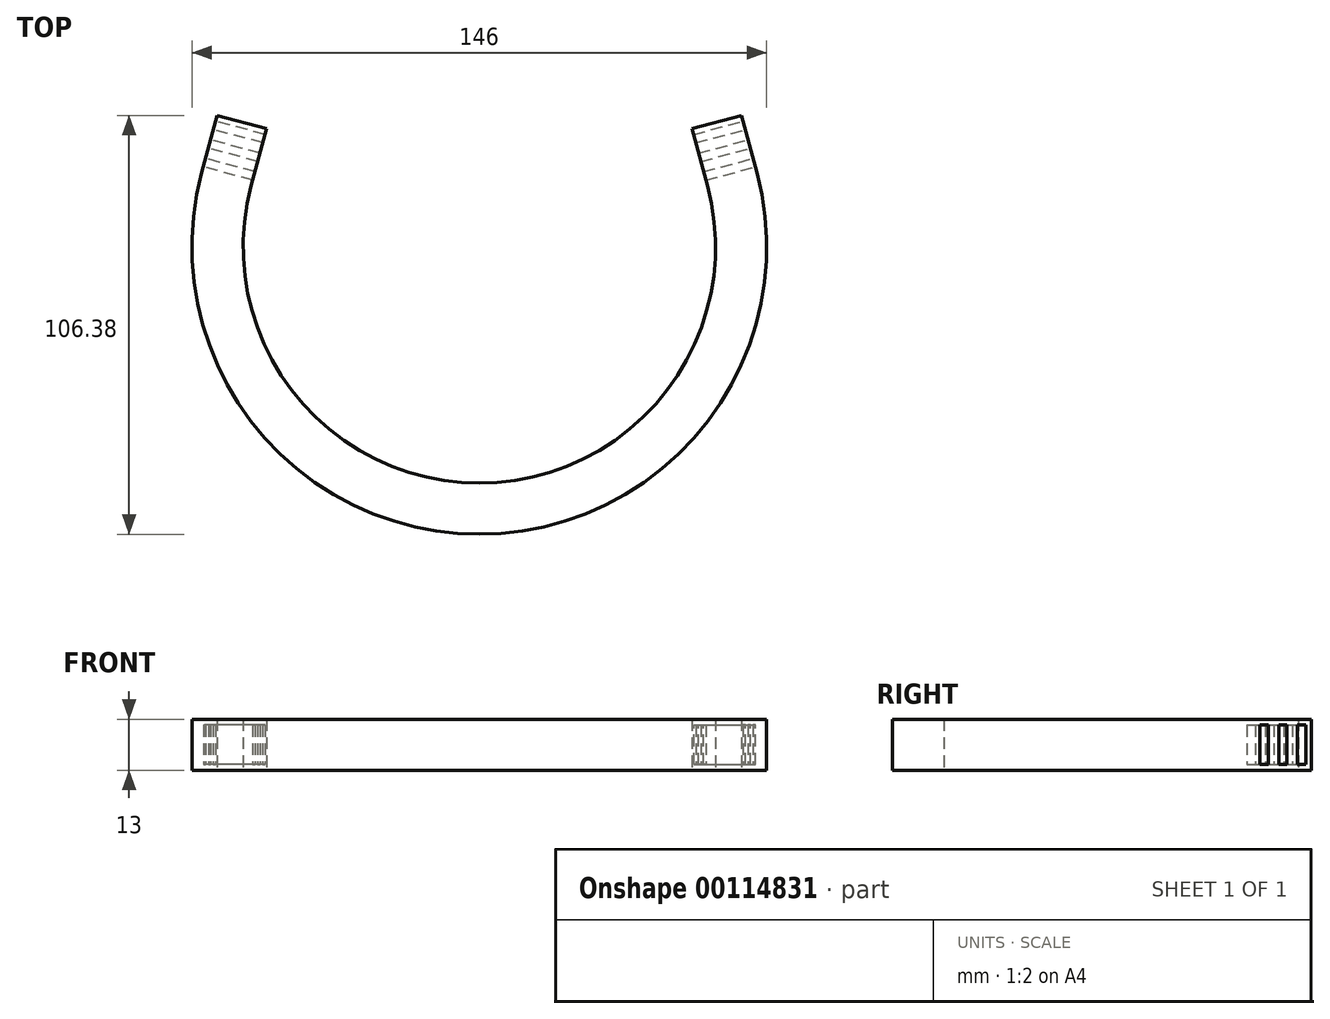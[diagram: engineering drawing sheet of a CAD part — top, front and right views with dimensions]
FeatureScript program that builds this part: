
annotation { "Feature Type Name" : "Feature", "Feature Type Description" : "" }
export const myFeature = defineFeature(function(context is Context, id is Id, definition is map)
    precondition{}
    {
        {
            var Q0;
            Q0=qCreatedBy(makeId("Top.planeOp"),FACE);
            var sketch = newSketch(context, id + "F0", { "sketchPlane" : qUnion([Q0])});
            skArc(sketch, "E0", {"start": v(-57.96, 15.53) * mm, "mid": v(0, -60) * mm, "end": v(57.96, 15.53) * mm});
            skArc(sketch, "E1.0", {"start": v(-70.51, 18.9) * mm, "mid": v(0, -73) * mm, "end": v(70.51, 18.9) * mm});
            skLineSegment(sketch, "E2", {"start": v(0, 0) * mm, "end": v(57.96, 15.53) * mm, "construction": true});
            skLineSegment(sketch, "E3.MirrorCS", {"start": v(0, 0) * mm, "end": v(-57.96, 15.53) * mm, "construction": true});
            skLineSegment(sketch, "E4", {"start": v(-70.51, 18.9) * mm, "end": v(-66.63, 33.38) * mm});
            skLineSegment(sketch, "E5", {"start": v(-57.96, 15.53) * mm, "end": v(-54.07, 30.02) * mm});
            skLineSegment(sketch, "E6", {"start": v(-54.07, 30.02) * mm, "end": v(-66.63, 33.38) * mm});
            skLineSegment(sketch, "E7.MirrorCS", {"start": v(54.07, 30.02) * mm, "end": v(66.63, 33.38) * mm});
            skLineSegment(sketch, "E8.MirrorCS", {"start": v(57.96, 15.53) * mm, "end": v(54.07, 30.02) * mm});
            skLineSegment(sketch, "E9.MirrorCS", {"start": v(70.51, 18.9) * mm, "end": v(66.63, 33.38) * mm});
            skLineSegment(sketch, "E10.trimOffspring", {"start": v(70.51, 18.9) * mm, "end": v(130.04, 34.84) * mm, "construction": true});
            skLineSegment(sketch, "E11.trimOffspring", {"start": v(-70.51, 18.9) * mm, "end": v(-130.04, 34.84) * mm, "construction": true});
            skSolve(sketch);
        }
        {
            var Q0;
            Q0=makeQuery(id+"F0.imprint","IMPRINT",FACE,{"disambiguationData":[TD([[makeQuery(id+"F0.imprint","IMPRINT",EDGE,{"derivedFrom":sQuery(id+"F0.wireOp",EDGE,"E1.0")}),1.0]])]});
            extrude(context, id + "F1", {"entities" : qUnion([Q0]), "depth" : 13 * mm});
        }
        {
            var Q0;
            Q0=makeQuery(id+"F1.opExtrude","SWEPT_FACE",FACE,{"disambiguationData":[OSD([sQuery(id+"F0.wireOp",EDGE,"E9.MirrorCS")])]});
            var sketch = newSketch(context, id + "F2", { "sketchPlane" : qUnion([Q0])});
            skLineSegment(sketch, "E12", {"start": v(12.98, 7.6) * mm, "end": v(12.98, 5.4) * mm});
            skLineSegment(sketch, "E13", {"start": v(0, 5.4) * mm, "end": v(0, 7.6) * mm});
            skLineSegment(sketch, "E14", {"start": v(1.5, 7.6) * mm, "end": v(1.5, 11.5) * mm});
            skLineSegment(sketch, "E15", {"start": v(1.5, 11.5) * mm, "end": v(3.7, 11.5) * mm});
            skLineSegment(sketch, "E16", {"start": v(3.7, 11.5) * mm, "end": v(3.7, 7.6) * mm});
            skLineSegment(sketch, "E17", {"start": v(3.7, 7.6) * mm, "end": v(3.7, 1.5) * mm});
            skLineSegment(sketch, "E18", {"start": v(3.7, 1.5) * mm, "end": v(1.5, 1.5) * mm});
            skLineSegment(sketch, "E19", {"start": v(1.5, 1.5) * mm, "end": v(1.5, 7.6) * mm});
            skLineSegment(sketch, "E20", {"start": v(-2.01, 6.5) * mm, "end": v(21.6, 6.5) * mm, "construction": true});
            skPoint(sketch, "E20.startSnap0", {"position": v(0, 6.5) * mm});
            skLineSegment(sketch, "E21.1.0.0", {"start": v(6.4, 11.5) * mm, "end": v(8.6, 11.5) * mm});
            skLineSegment(sketch, "E21.1.0.1", {"start": v(8.6, 11.5) * mm, "end": v(8.6, 7.6) * mm});
            skLineSegment(sketch, "E21.1.0.2", {"start": v(8.6, 7.6) * mm, "end": v(8.6, 1.5) * mm});
            skLineSegment(sketch, "E21.1.0.3", {"start": v(6.4, 1.5) * mm, "end": v(6.4, 7.6) * mm});
            skLineSegment(sketch, "E21.1.0.4", {"start": v(6.4, 7.6) * mm, "end": v(6.4, 11.5) * mm});
            skLineSegment(sketch, "E21.1.0.5", {"start": v(8.6, 1.5) * mm, "end": v(6.4, 1.5) * mm});
            skLineSegment(sketch, "E21.2.0.0", {"start": v(11.3, 11.5) * mm, "end": v(13.5, 11.5) * mm});
            skLineSegment(sketch, "E21.2.0.1", {"start": v(13.5, 11.5) * mm, "end": v(13.5, 7.6) * mm});
            skLineSegment(sketch, "E21.2.0.2", {"start": v(13.5, 7.6) * mm, "end": v(13.5, 1.5) * mm});
            skLineSegment(sketch, "E21.2.0.3", {"start": v(11.3, 1.5) * mm, "end": v(11.3, 7.6) * mm});
            skLineSegment(sketch, "E21.2.0.4", {"start": v(11.3, 7.6) * mm, "end": v(11.3, 11.5) * mm});
            skLineSegment(sketch, "E21.2.0.5", {"start": v(13.5, 1.5) * mm, "end": v(11.3, 1.5) * mm});
            skLineSegment(sketch, "E21.direction1", {"start": v(1.5, 11.5) * mm, "end": v(6.4, 11.5) * mm, "construction": true});
            skLineSegment(sketch, "E22.MirrorCS", {"start": v(531.38, 11.5) * mm, "end": v(531.38, 7.6) * mm});
            skLineSegment(sketch, "E23.MirrorCS", {"start": v(533.58, 11.5) * mm, "end": v(531.38, 11.5) * mm});
            skLineSegment(sketch, "E24.MirrorCS", {"start": v(533.58, 7.6) * mm, "end": v(533.58, 11.5) * mm});
            skLineSegment(sketch, "E25.MirrorCS", {"start": v(541.18, 11.5) * mm, "end": v(541.18, 7.6) * mm});
            skLineSegment(sketch, "E26.MirrorCS", {"start": v(546.9, 6.5) * mm, "end": v(523.29, 6.5) * mm, "construction": true});
            skLineSegment(sketch, "E27.MirrorCS", {"start": v(531.9, 5.4) * mm, "end": v(544.88, 5.4) * mm});
            skLineSegment(sketch, "E28.MirrorCS", {"start": v(541.18, 7.6) * mm, "end": v(541.18, 1.5) * mm});
            skLineSegment(sketch, "E29.MirrorCS", {"start": v(541.18, 1.5) * mm, "end": v(543.38, 1.5) * mm});
            skLineSegment(sketch, "E30.MirrorCS", {"start": v(543.38, 1.5) * mm, "end": v(543.38, 7.6) * mm});
            skLineSegment(sketch, "E31.MirrorCS", {"start": v(536.28, 1.5) * mm, "end": v(538.48, 1.5) * mm});
            skSolve(sketch);
        }
        {
            var Q0;
            Q0 = qSketchRegion(id + "F2", true);
            extrude(context, id + "F3", {"entities" : qUnion([Q0]), "operationType" : NewBodyOperationType.REMOVE, "oppositeDirection" : true, "depth" : 25 * mm});
        }
        {
            var Q0;
            Q0=makeQuery(id+"F1.opExtrude","SWEPT_FACE",FACE,{"disambiguationData":[OSD([sQuery(id+"F0.wireOp",EDGE,"E4")])]});
            var sketch = newSketch(context, id + "F4", { "sketchPlane" : qUnion([Q0])});
            skLineSegment(sketch, "E32", {"start": v(0, 6.5) * mm, "end": v(-19.25, 6.5) * mm, "construction": true});
            skPoint(sketch, "E32.endSnap0", {"position": v(-15, 6.5) * mm});
            skLineSegment(sketch, "E33.left", {"start": v(0, 7.6) * mm, "end": v(0, 5.4) * mm});
            skLineSegment(sketch, "E33.right", {"start": v(-12.8, 7.6) * mm, "end": v(-12.8, 5.4) * mm});
            skLineSegment(sketch, "E34.bottom", {"start": v(-1.5, 11.5) * mm, "end": v(-3.7, 11.5) * mm});
            skLineSegment(sketch, "E34.top", {"start": v(-1.5, 1.5) * mm, "end": v(-3.7, 1.5) * mm});
            skLineSegment(sketch, "E34.left", {"start": v(-1.5, 11.5) * mm, "end": v(-1.5, 1.5) * mm});
            skLineSegment(sketch, "E34.right", {"start": v(-3.7, 11.5) * mm, "end": v(-3.7, 1.5) * mm});
            skLineSegment(sketch, "E35.1.0.0", {"start": v(-8.6, 11.5) * mm, "end": v(-8.6, 1.5) * mm});
            skLineSegment(sketch, "E35.1.0.1", {"start": v(-6.4, 11.5) * mm, "end": v(-8.6, 11.5) * mm});
            skLineSegment(sketch, "E35.1.0.2", {"start": v(-6.4, 11.5) * mm, "end": v(-6.4, 1.5) * mm});
            skLineSegment(sketch, "E35.1.0.3", {"start": v(-6.4, 1.5) * mm, "end": v(-8.6, 1.5) * mm});
            skLineSegment(sketch, "E35.2.0.0", {"start": v(-13.5, 11.5) * mm, "end": v(-13.5, 1.5) * mm});
            skLineSegment(sketch, "E35.2.0.1", {"start": v(-11.3, 11.5) * mm, "end": v(-13.5, 11.5) * mm});
            skLineSegment(sketch, "E35.2.0.2", {"start": v(-11.3, 11.5) * mm, "end": v(-11.3, 1.5) * mm});
            skLineSegment(sketch, "E35.2.0.3", {"start": v(-11.3, 1.5) * mm, "end": v(-13.5, 1.5) * mm});
            skLineSegment(sketch, "E35.direction1", {"start": v(-3.7, 1.5) * mm, "end": v(-8.6, 1.5) * mm, "construction": true});
            skSolve(sketch);
        }
        {
            var Q0;
            Q0 = qSketchRegion(id + "F4", true);
            extrude(context, id + "F5", {"entities" : qUnion([Q0]), "operationType" : NewBodyOperationType.REMOVE, "oppositeDirection" : true, "depth" : 25 * mm});
        }
    });
